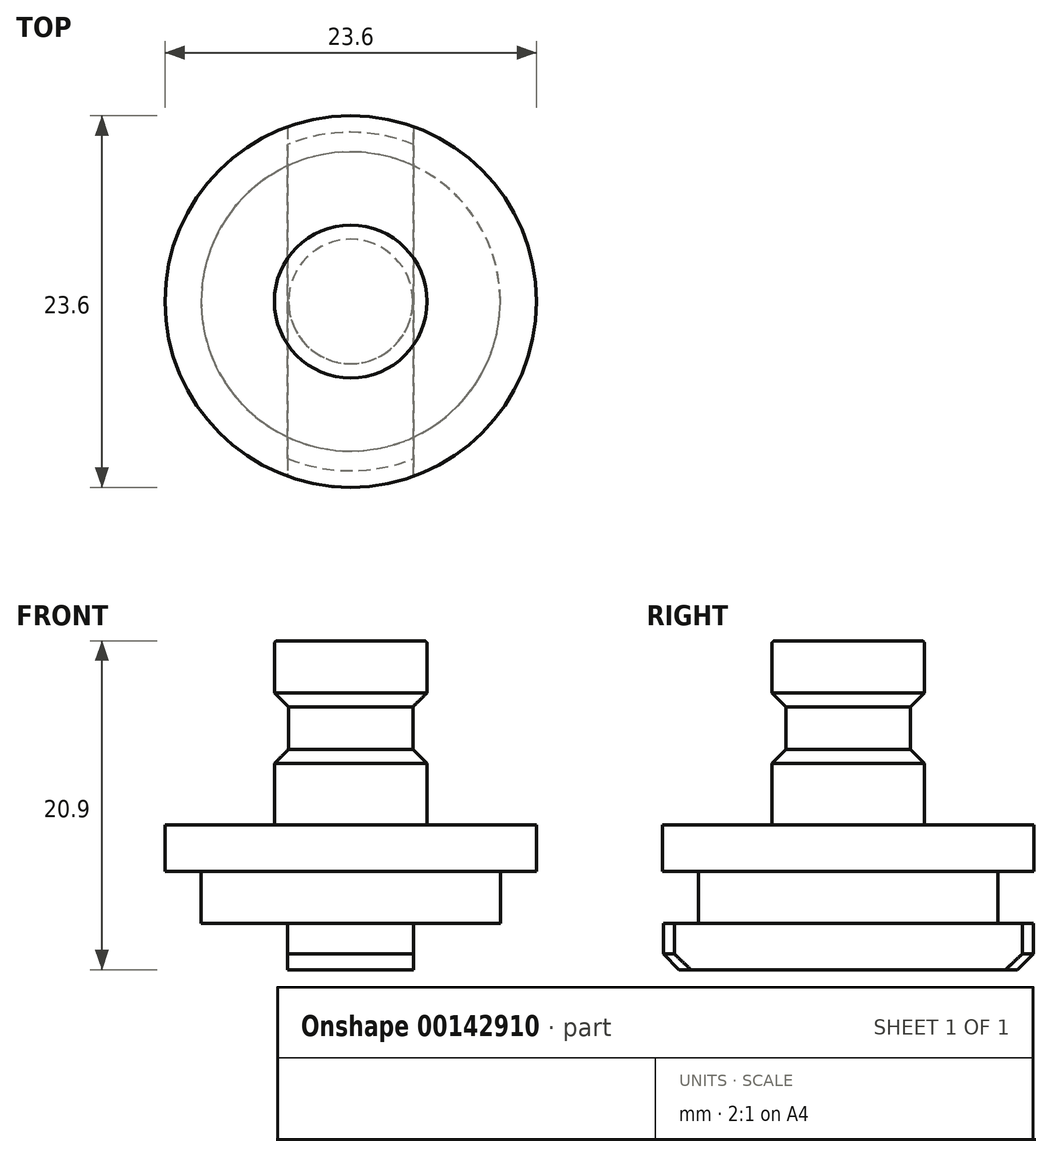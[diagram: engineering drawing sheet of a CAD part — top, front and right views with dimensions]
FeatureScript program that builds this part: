
annotation { "Feature Type Name" : "Feature", "Feature Type Description" : "" }
export const myFeature = defineFeature(function(context is Context, id is Id, definition is map)
    precondition{}
    {
        {
            var Q0;
            Q0=qCreatedBy(makeId("Front.planeOp"),FACE);
            var sketch = newSketch(context, id + "F0", { "sketchPlane" : qUnion([Q0])});
            skLineSegment(sketch, "E0", {"start": v(0, 0) * mm, "end": v(-11.75, 0) * mm});
            skLineSegment(sketch, "E1", {"start": v(-11.75, 0) * mm, "end": v(-11.75, 2.95) * mm});
            skLineSegment(sketch, "E2", {"start": v(-11.75, 2.95) * mm, "end": v(-9.5, 2.95) * mm});
            skLineSegment(sketch, "E3", {"start": v(-9.5, 2.95) * mm, "end": v(-9.5, 6.25) * mm});
            skLineSegment(sketch, "E4", {"start": v(-9.5, 6.25) * mm, "end": v(-11.8, 6.25) * mm});
            skLineSegment(sketch, "E5", {"start": v(-11.8, 6.25) * mm, "end": v(-11.8, 9.2) * mm});
            skLineSegment(sketch, "E6", {"start": v(-11.8, 9.2) * mm, "end": v(-4.85, 9.2) * mm});
            skLineSegment(sketch, "E7", {"start": v(-4.85, 9.2) * mm, "end": v(-4.85, 14.1) * mm});
            skLineSegment(sketch, "E8", {"start": v(-4.85, 14.1) * mm, "end": v(-3.95, 14.1) * mm});
            skLineSegment(sketch, "E9", {"start": v(-3.95, 14.1) * mm, "end": v(-3.95, 16.6) * mm});
            skLineSegment(sketch, "E10", {"start": v(-3.95, 16.6) * mm, "end": v(-4.85, 16.6) * mm});
            skLineSegment(sketch, "E11", {"start": v(-4.85, 16.6) * mm, "end": v(-4.85, 20.9) * mm});
            skLineSegment(sketch, "E12", {"start": v(-4.85, 20.9) * mm, "end": v(0, 20.9) * mm});
            skLineSegment(sketch, "E13", {"start": v(0, 20.9) * mm, "end": v(0, 0) * mm});
            skSolve(sketch);
        }
        {
            var Q0;
            Q0 = qSketchRegion(id + "F0", true);
            var Q1;
            Q1=sQuery(id+"F0.wireOp",EDGE,"E13");
            revolve(context, id + "F1", {"entities" : qUnion([Q0]), "axis" : qUnion([Q1]), "revolveType" : RevolveType.FULL});
        }
        {
            var Q0;
            Q0=makeQuery(id+"F1.opRevolve","SWEPT_FACE",FACE,{"disambiguationData":[OSD([sQuery(id+"F0.wireOp",EDGE,"E0")])]});
            var sketch = newSketch(context, id + "F2", { "sketchPlane" : qUnion([Q0])});
            skLineSegment(sketch, "E14", {"start": v(-4, 11.05) * mm, "end": v(-4, -11.05) * mm});
            skLineSegment(sketch, "E15", {"start": v(4, 11.05) * mm, "end": v(4, -11.05) * mm});
            skSolve(sketch);
        }
        {
            var Q0;
            {var subQ0=sQuery(id+"F2.wireOp",EDGE,"E14");Q0=makeQuery(id+"F2.imprint","IMPRINT",FACE,{"disambiguationData":[TD([[makeQuery(id+"F2.imprint","IMPRINT",EDGE,{"derivedFrom":subQ0}),-1.0]])]});}
            var Q1;
            {var subQ0=sQuery(id+"F2.wireOp",EDGE,"E15");Q1=makeQuery(id+"F2.imprint","IMPRINT",FACE,{"disambiguationData":[TD([[makeQuery(id+"F2.imprint","IMPRINT",EDGE,{"derivedFrom":subQ0}),1.0]])]});}
            var Q2;
            Q2=makeQuery(id+"F1.opRevolve","SWEPT_FACE",FACE,{"disambiguationData":[OSD([sQuery(id+"F0.wireOp",EDGE,"E2")])]});
            extrude(context, id + "F3", {"entities" : qUnion([Q0, Q1]), "operationType" : NewBodyOperationType.REMOVE, "endBound" : BoundingType.UP_TO_SURFACE, "oppositeDirection" : true, "endBoundEntityFace" : qUnion([Q2]), "depth" : 25 * mm});
        }
        {
            var Q0;
            Q0=makeQuery(id+"F3.boolean.opBoolean","SPLIT",EDGE,{"disambiguationData":[OD(0.0)],"derivedFrom":makeQuery(id+"F1.opRevolve","SWEPT_EDGE",EDGE,{"disambiguationData":[OSD([sQuery(id+"F0.wireOp",EDGE,"E0"),sQuery(id+"F0.wireOp",EDGE,"E1")])]})});
            var Q1;
            Q1=makeQuery(id+"F3.boolean.opBoolean","SPLIT",EDGE,{"disambiguationData":[OD(1.0)],"derivedFrom":makeQuery(id+"F1.opRevolve","SWEPT_EDGE",EDGE,{"disambiguationData":[OSD([sQuery(id+"F0.wireOp",EDGE,"E0"),sQuery(id+"F0.wireOp",EDGE,"E1")])]})});
            var Q2;
            Q2=makeQuery(id+"F1.opRevolve","SWEPT_EDGE",EDGE,{"disambiguationData":[OSD([sQuery(id+"F0.wireOp",EDGE,"E10"),sQuery(id+"F0.wireOp",EDGE,"E11")])]});
            var Q3;
            Q3=makeQuery(id+"F1.opRevolve","SWEPT_EDGE",EDGE,{"disambiguationData":[OSD([sQuery(id+"F0.wireOp",EDGE,"E7"),sQuery(id+"F0.wireOp",EDGE,"E8")])]});
            chamfer(context, id + "F4", {"entities" : qUnion([Q0, Q1, Q2, Q3]), "chamferType" : ChamferType.OFFSET_ANGLE, "width" : 1 * mm, "oppositeDirection" : false, "angle" : 45 * degree, "tangentPropagation" : true});
        }
        {
            var Q0;
            Q0=makeQuery(id+"F1.opRevolve","SWEPT_EDGE",EDGE,{"disambiguationData":[OSD([sQuery(id+"F0.wireOp",EDGE,"E11"),sQuery(id+"F0.wireOp",EDGE,"E12")])]});
            fillet(context, id + "F5", {"entities" : qUnion([Q0]), "radius" : 0.2 * mm, "tangentPropagation" : true, "allowEdgeOverflow" : false});
        }
    });
